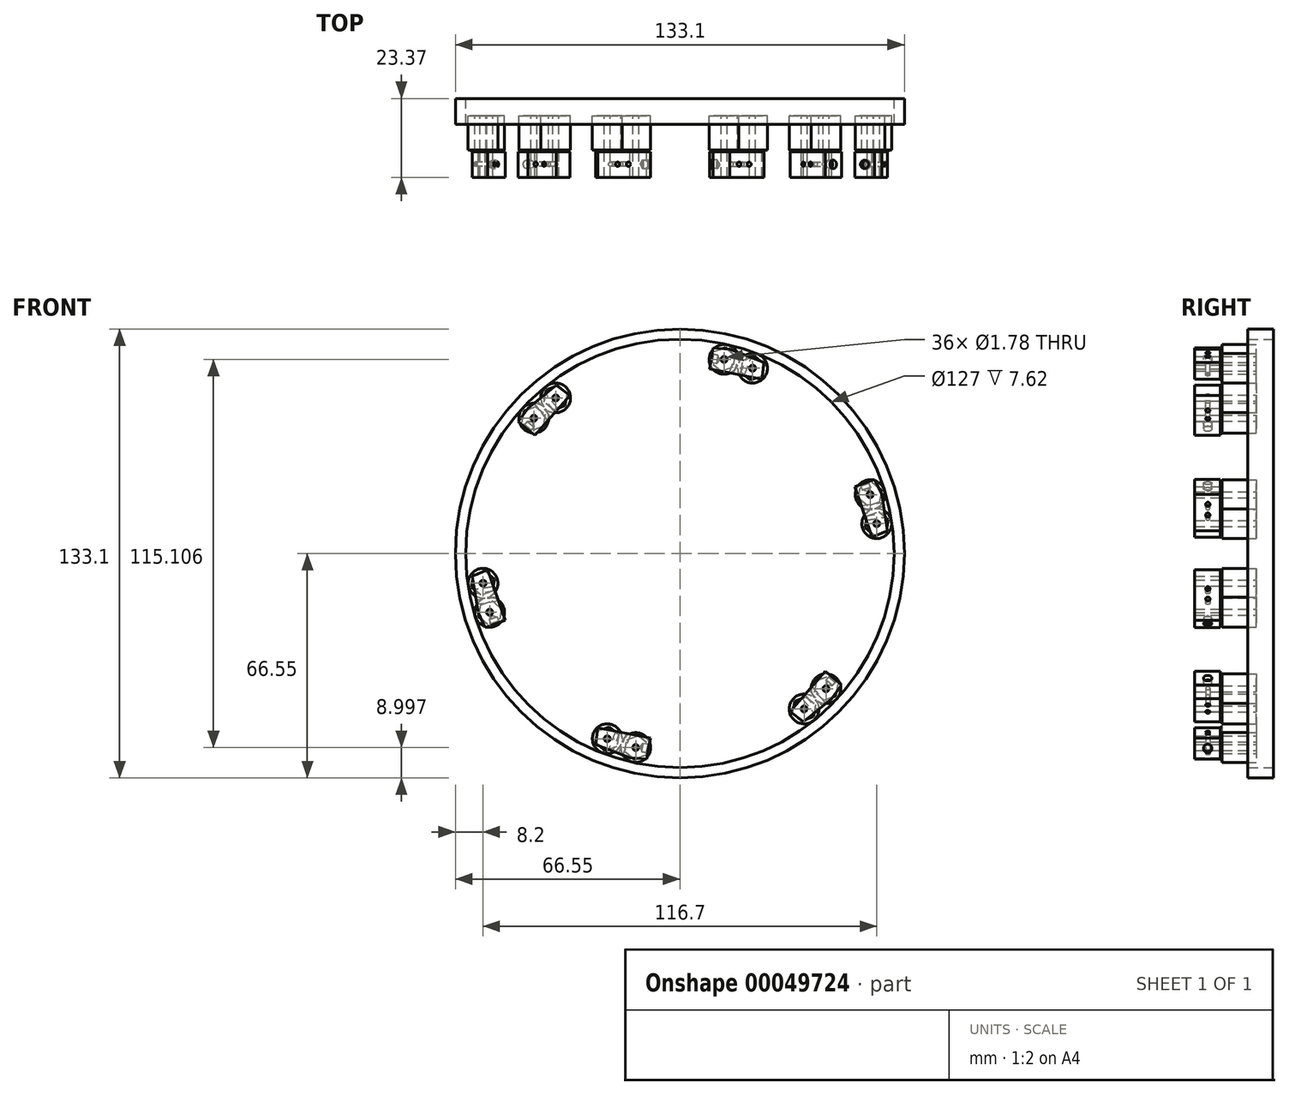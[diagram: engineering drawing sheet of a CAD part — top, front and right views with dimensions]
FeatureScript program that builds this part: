
annotation { "Feature Type Name" : "Feature", "Feature Type Description" : "" }
export const myFeature = defineFeature(function(context is Context, id is Id, definition is map)
    precondition{}
    {
        {
            var Q0;
            Q0=qCreatedBy(makeId("Front.planeOp"),FACE);
            var sketch = newSketch(context, id + "F0", { "sketchPlane" : qUnion([Q0])});
            skCircle(sketch, "E0", {"center": v(0, 0) * mm, "radius": 66.55 * mm});
            skSolve(sketch);
        }
        {
            var Q0;
            Q0=makeQuery(id+"F0.imprint","IMPRINT",FACE,{"disambiguationData":[TD([[makeQuery(id+"F0.imprint","IMPRINT",EDGE,{"derivedFrom":sQuery(id+"F0.wireOp",EDGE,"E0")}),1.0]])]});
            extrude(context, id + "F1", {"entities" : qUnion([Q0]), "depth" : 7.62 * mm});
        }
        {
            var Q0;
            Q0=sQuery(id+"F0.wireOp",VERTEX,"E0.center");
            var Q1;
            Q1=makeQuery(id+"F1.opExtrude","SWEPT_BODY",BODY,{"disambiguationData":[OSD([sQuery(id+"F0.wireOp",EDGE,"E0")])]});
            hole(context, id + "F2", {"style" : HoleStyle.SIMPLE, "holeDiameter" : 127 * mm, "endStyle" : HoleEndStyle.THROUGH, "oppositeDirection" : true, "locations" : qUnion([Q0]), "scope" : qUnion([Q1])});
        }
        {
            var Q0;
            Q0=qCreatedBy(makeId("Front.planeOp"),FACE);
            var sketch = newSketch(context, id + "F3", { "sketchPlane" : qUnion([Q0])});
            skCircle(sketch, "E1", {"center": v(13.1, 57.55) * mm, "radius": 4.4 * mm});
            skPoint(sketch, "E1.first.point", {"position": v(14.07, 61.85) * mm});
            skPoint(sketch, "E1.second.point", {"position": v(11.49, 53.45) * mm});
            skPoint(sketch, "E1.third.point", {"position": v(11.97, 53.29) * mm});
            skCircle(sketch, "E2", {"center": v(21.53, 54.95) * mm, "radius": 4.4 * mm});
            skSolve(sketch);
        }
        {
            var Q0;
            Q0=makeQuery(id+"F3.imprint","IMPRINT",FACE,{"disambiguationData":[TD([[makeQuery(id+"F3.imprint","IMPRINT",EDGE,{"derivedFrom":sQuery(id+"F3.wireOp",EDGE,"E2")}),1.0]])]});
            var Q1;
            Q1=makeQuery(id+"F3.imprint","IMPRINT",FACE,{"disambiguationData":[TD([[makeQuery(id+"F3.imprint","IMPRINT",EDGE,{"derivedFrom":sQuery(id+"F3.wireOp",EDGE,"E1")}),1.0]])]});
            extrude(context, id + "F4", {"entities" : qUnion([Q0, Q1]), "depth" : 15.24 * mm, "hasSecondDirection" : true, "secondDirectionOppositeDirection" : false, "secondDirectionDepth" : 5.08 * mm});
        }
        {
            var Q0;
            Q0=makeQuery(id+"F4.opExtrude","CAP_FACE",FACE,{"disambiguationData":[OSD([sQuery(id+"F3.wireOp",EDGE,"E2")])],"isStart":false});
            var sketch = newSketch(context, id + "F5", { "sketchPlane" : qUnion([Q0])});
            skCircle(sketch, "E3.cCircle", {"center": v(21.53, 54.95) * mm, "radius": 3.13 * mm, "construction": true});
            skLineSegment(sketch, "E3.0", {"start": v(24.3, 52.62) * mm, "end": v(20.9, 51.39) * mm});
            skLineSegment(sketch, "E3.1", {"start": v(20.9, 51.39) * mm, "end": v(18.14, 53.71) * mm});
            skLineSegment(sketch, "E3.2", {"start": v(18.14, 53.71) * mm, "end": v(18.77, 57.27) * mm});
            skLineSegment(sketch, "E3.3", {"start": v(18.77, 57.27) * mm, "end": v(22.16, 58.5) * mm});
            skLineSegment(sketch, "E3.4", {"start": v(22.16, 58.5) * mm, "end": v(24.93, 56.18) * mm});
            skLineSegment(sketch, "E3.5", {"start": v(24.93, 56.18) * mm, "end": v(24.3, 52.62) * mm});
            skPoint(sketch, "E3.0.midPoint", {"position": v(22.6, 52) * mm});
            skLineSegment(sketch, "E4.1", {"start": v(12.3, 54) * mm, "end": v(9.52, 56.32) * mm});
            skLineSegment(sketch, "E4.2", {"start": v(9.52, 56.32) * mm, "end": v(10.16, 59.88) * mm});
            skLineSegment(sketch, "E4.3", {"start": v(10.16, 59.88) * mm, "end": v(13.55, 61.11) * mm});
            skLineSegment(sketch, "E4.4", {"start": v(13.55, 61.11) * mm, "end": v(16.32, 58.79) * mm});
            skLineSegment(sketch, "E4.5", {"start": v(16.32, 58.79) * mm, "end": v(15.69, 55.23) * mm});
            skLineSegment(sketch, "E4.0", {"start": v(15.69, 55.23) * mm, "end": v(12.3, 54) * mm});
            skCircle(sketch, "E4.cCircle", {"center": v(12.92, 57.55) * mm, "radius": 3.13 * mm, "construction": true});
            skSolve(sketch);
        }
        {
            var Q0;
            Q0=makeQuery(id+"F5.imprint","IMPRINT",FACE,{"disambiguationData":[TD([[makeQuery(id+"F5.imprint","IMPRINT",EDGE,{"derivedFrom":sQuery(id+"F5.wireOp",EDGE,"E3.0")}),-1.0]])]});
            var Q1;
            Q1=makeQuery(id+"F5.imprint","IMPRINT",FACE,{"disambiguationData":[TD([[makeQuery(id+"F5.imprint","IMPRINT",EDGE,{"derivedFrom":sQuery(id+"F5.wireOp",EDGE,"E4.1")}),-1.0]])]});
            extrude(context, id + "F6", {"entities" : qUnion([Q0, Q1]), "depth" : 0.5 * mm});
        }
        {
            var Q0;
            Q0=makeQuery(id+"F6.opExtrude","CAP_FACE",FACE,{"disambiguationData":[OSD([sQuery(id+"F5.wireOp",EDGE,"E3.0"),sQuery(id+"F5.wireOp",EDGE,"E3.1"),sQuery(id+"F5.wireOp",EDGE,"E3.2"),sQuery(id+"F5.wireOp",EDGE,"E3.3"),sQuery(id+"F5.wireOp",EDGE,"E3.4"),sQuery(id+"F5.wireOp",EDGE,"E3.5")])],"isStart":false});
            var sketch = newSketch(context, id + "F7", { "sketchPlane" : qUnion([Q0])});
            skLineSegment(sketch, "E5", {"start": v(24.3, 51.72) * mm, "end": v(24.93, 56.67) * mm});
            skLineSegment(sketch, "E6", {"start": v(24.93, 56.67) * mm, "end": v(14.76, 60.55) * mm});
            skLineSegment(sketch, "E7", {"start": v(14.76, 60.55) * mm, "end": v(9.87, 61) * mm});
            skLineSegment(sketch, "E8", {"start": v(9.87, 61) * mm, "end": v(8.76, 54.78) * mm});
            skLineSegment(sketch, "E9", {"start": v(8.76, 54.78) * mm, "end": v(24.3, 51.72) * mm});
            skSolve(sketch);
        }
        {
            var Q0;
            {var subQ8=sQuery(id+"F7.wireOp",EDGE,"E7");Q0=makeQuery(id+"F7.imprint","IMPRINT",FACE,{"disambiguationData":[TD([[makeQuery(id+"F7.imprint","IMPRINT",EDGE,{"derivedFrom":subQ8}),1.0]])]});}
            var Q1;
            {var subQ11=makeQuery(id+"F6.opExtrude","CAP_EDGE",EDGE,{"disambiguationData":[OSD([sQuery(id+"F5.wireOp",EDGE,"E3.2")])],"isStart":false});Q1=makeQuery(id+"F7.imprint","IMPRINT",FACE,{"disambiguationData":[TD([[makeQuery(id+"F7.imprint","IMPRINT",EDGE,{"derivedFrom":subQ11}),-1.0]])]});}
            var Q2;
            {var subQ1=sQuery(id+"F7.wireOp",EDGE,"E5");var subQ5=sQuery(id+"F7.wireOp",EDGE,"E9");var subQ7=makeQuery(id+"F7.imprint","INTERSECT",VERTEX,{"derivedFrom":[subQ1,subQ5]});Q2=makeQuery(id+"F7.imprint","IMPRINT",FACE,{"disambiguationData":[TD([[makeQuery(id+"F7.imprint","IMPRINT",EDGE,{"disambiguationData":[TD([[subQ7,-1.0]])],"derivedFrom":subQ1}),1.0]])]});}
            var Q3;
            {var subQ1=sQuery(id+"F7.wireOp",EDGE,"E6");var subQ3=sQuery(id+"F7.wireOp",EDGE,"E5");var subQ5=makeQuery(id+"F7.imprint","INTERSECT",VERTEX,{"derivedFrom":[subQ3,subQ1]});Q3=makeQuery(id+"F7.imprint","IMPRINT",FACE,{"disambiguationData":[TD([[makeQuery(id+"F7.imprint","IMPRINT",EDGE,{"disambiguationData":[TD([[subQ5,1.0]])],"derivedFrom":subQ3}),1.0]])]});}
            extrude(context, id + "F8", {"entities" : qUnion([Q0, Q1, Q2, Q3]), "depth" : 7.62 * mm});
        }
        {
            var Q0;
            Q0=sQuery(id+"F3.wireOp",VERTEX,"E2.center");
            var Q1;
            Q1=makeQuery(id+"F4.opExtrude","SWEPT_BODY",BODY,{"disambiguationData":[OSD([sQuery(id+"F3.wireOp",EDGE,"E2")])]});
            var Q2;
            Q2=makeQuery(id+"F6.opExtrude","SWEPT_BODY",BODY,{"disambiguationData":[OSD([sQuery(id+"F5.wireOp",EDGE,"E3.0"),sQuery(id+"F5.wireOp",EDGE,"E3.1"),sQuery(id+"F5.wireOp",EDGE,"E3.2"),sQuery(id+"F5.wireOp",EDGE,"E3.3"),sQuery(id+"F5.wireOp",EDGE,"E3.4"),sQuery(id+"F5.wireOp",EDGE,"E3.5")])]});
            var Q3;
            Q3=makeQuery(id+"F8.opExtrude","SWEPT_BODY",BODY,{"disambiguationData":[OSD([sQuery(id+"F7.wireOp",EDGE,"E5"),sQuery(id+"F7.wireOp",EDGE,"E6"),sQuery(id+"F7.wireOp",EDGE,"E7"),sQuery(id+"F7.wireOp",EDGE,"E8"),sQuery(id+"F7.wireOp",EDGE,"E9")])]});
            hole(context, id + "F9", {"style" : HoleStyle.SIMPLE, "holeDiameter" : 1.78 * mm, "endStyle" : HoleEndStyle.THROUGH, "oppositeDirection" : true, "locations" : qUnion([Q0]), "scope" : qUnion([Q1, Q2, Q3])});
        }
        {
            var Q0;
            Q0=sQuery(id+"F3.wireOp",VERTEX,"E1.center");
            var Q1;
            Q1=makeQuery(id+"F4.opExtrude","SWEPT_BODY",BODY,{"disambiguationData":[OSD([sQuery(id+"F3.wireOp",EDGE,"E1")])]});
            var Q2;
            Q2=makeQuery(id+"F6.opExtrude","SWEPT_BODY",BODY,{"disambiguationData":[OSD([sQuery(id+"F5.wireOp",EDGE,"E4.1"),sQuery(id+"F5.wireOp",EDGE,"E4.2"),sQuery(id+"F5.wireOp",EDGE,"E4.3"),sQuery(id+"F5.wireOp",EDGE,"E4.4"),sQuery(id+"F5.wireOp",EDGE,"E4.5"),sQuery(id+"F5.wireOp",EDGE,"E4.0")])]});
            var Q3;
            Q3=makeQuery(id+"F8.opExtrude","SWEPT_BODY",BODY,{"disambiguationData":[OSD([sQuery(id+"F7.wireOp",EDGE,"E5"),sQuery(id+"F7.wireOp",EDGE,"E6"),sQuery(id+"F7.wireOp",EDGE,"E7"),sQuery(id+"F7.wireOp",EDGE,"E8"),sQuery(id+"F7.wireOp",EDGE,"E9")])]});
            hole(context, id + "F10", {"style" : HoleStyle.SIMPLE, "holeDiameter" : 1.78 * mm, "endStyle" : HoleEndStyle.THROUGH, "oppositeDirection" : true, "locations" : qUnion([Q0]), "scope" : qUnion([Q1, Q2, Q3])});
        }
        {
            var Q0;
            Q0=makeQuery(id+"F8.opExtrude","SWEPT_FACE",FACE,{"disambiguationData":[OSD([sQuery(id+"F7.wireOp",EDGE,"E6")])]});
            var sketch = newSketch(context, id + "F11", { "sketchPlane" : qUnion([Q0])});
            skCircle(sketch, "E10", {"center": v(-4.86, -19.5) * mm, "radius": 0.82 * mm});
            skCircle(sketch, "E11", {"center": v(-1.64, -19.51) * mm, "radius": 0.82 * mm});
            skSolve(sketch);
        }
        {
            var Q0;
            Q0=sQuery(id+"F11.wireOp",VERTEX,"E10.center");
            var Q1;
            Q1=sQuery(id+"F11.wireOp",VERTEX,"E11.center");
            var Q2;
            Q2=makeQuery(id+"F8.opExtrude","SWEPT_BODY",BODY,{"disambiguationData":[OSD([sQuery(id+"F7.wireOp",EDGE,"E5"),sQuery(id+"F7.wireOp",EDGE,"E6"),sQuery(id+"F7.wireOp",EDGE,"E7"),sQuery(id+"F7.wireOp",EDGE,"E8"),sQuery(id+"F7.wireOp",EDGE,"E9")])]});
            hole(context, id + "F12", {"style" : HoleStyle.SIMPLE, "holeDiameter" : 1.27 * mm, "endStyle" : HoleEndStyle.THROUGH, "locations" : qUnion([Q0, Q1]), "scope" : qUnion([Q2])});
        }
        {
            var Q0;
            Q0=makeQuery(id+"F8.opExtrude","SWEPT_FACE",FACE,{"disambiguationData":[OSD([sQuery(id+"F7.wireOp",EDGE,"E8")])]});
            var sketch = newSketch(context, id + "F13", { "sketchPlane" : qUnion([Q0])});
            skCircle(sketch, "E12", {"center": v(19.55, 58.57) * mm, "radius": 1.19 * mm});
            skSolve(sketch);
        }
        {
            var Q0;
            Q0=sQuery(id+"F13.wireOp",VERTEX,"E12.center");
            var Q1;
            Q1=makeQuery(id+"F8.opExtrude","SWEPT_BODY",BODY,{"disambiguationData":[OSD([sQuery(id+"F7.wireOp",EDGE,"E5"),sQuery(id+"F7.wireOp",EDGE,"E6"),sQuery(id+"F7.wireOp",EDGE,"E7"),sQuery(id+"F7.wireOp",EDGE,"E8"),sQuery(id+"F7.wireOp",EDGE,"E9")])]});
            hole(context, id + "F14", {"style" : HoleStyle.SIMPLE, "holeDiameter" : 2.54 * mm, "endStyle" : HoleEndStyle.BLIND, "holeDepth" : 1.78 * mm, "locations" : qUnion([Q0]), "scope" : qUnion([Q1])});
        }
        {
            var Q0;
            Q0=makeQuery(id+"F4.opExtrude","SWEPT_BODY",BODY,{"disambiguationData":[OSD([sQuery(id+"F3.wireOp",EDGE,"E1")])]});
            var Q1;
            Q1=makeQuery(id+"F4.opExtrude","SWEPT_BODY",BODY,{"disambiguationData":[OSD([sQuery(id+"F3.wireOp",EDGE,"E2")])]});
            var Q2;
            Q2=makeQuery(id+"F6.opExtrude","SWEPT_BODY",BODY,{"disambiguationData":[OSD([sQuery(id+"F5.wireOp",EDGE,"E4.1"),sQuery(id+"F5.wireOp",EDGE,"E4.2"),sQuery(id+"F5.wireOp",EDGE,"E4.3"),sQuery(id+"F5.wireOp",EDGE,"E4.4"),sQuery(id+"F5.wireOp",EDGE,"E4.5"),sQuery(id+"F5.wireOp",EDGE,"E4.0")])]});
            var Q3;
            Q3=makeQuery(id+"F6.opExtrude","SWEPT_BODY",BODY,{"disambiguationData":[OSD([sQuery(id+"F5.wireOp",EDGE,"E3.0"),sQuery(id+"F5.wireOp",EDGE,"E3.1"),sQuery(id+"F5.wireOp",EDGE,"E3.2"),sQuery(id+"F5.wireOp",EDGE,"E3.3"),sQuery(id+"F5.wireOp",EDGE,"E3.4"),sQuery(id+"F5.wireOp",EDGE,"E3.5")])]});
            var Q4;
            Q4=makeQuery(id+"F8.opExtrude","SWEPT_BODY",BODY,{"disambiguationData":[OSD([sQuery(id+"F7.wireOp",EDGE,"E5"),sQuery(id+"F7.wireOp",EDGE,"E6"),sQuery(id+"F7.wireOp",EDGE,"E7"),sQuery(id+"F7.wireOp",EDGE,"E8"),sQuery(id+"F7.wireOp",EDGE,"E9")])]});
            var Q5;
            Q5=sQuery(id+"F0.wireOp",EDGE,"E0");
            circularPattern(context, id + "F15", {"entities" : qUnion([Q0, Q1, Q2, Q3, Q4]), "axis" : qUnion([Q5]), "angle" : 60 * degree, "instanceCount" : round(6)});
        }
    });
